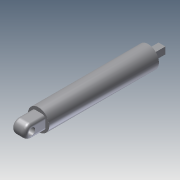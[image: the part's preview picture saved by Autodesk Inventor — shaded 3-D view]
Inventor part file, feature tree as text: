
AUTODESK INVENTOR PART (.ipt)
format: ipt  version: 2011 (Build 150239000, 239)  size: 170,496 bytes
history: native  units: in
note: dims shown in document units (in); Inventor stores cm internally (conversion verified against a paired STEP export)
features: extrude x11, sketch x11, fillet x2
ambient origin geometry x8: Origin, YZ Plane, XZ Plane, XY Plane, X Axis, Y Axis, Z Axis, Center Point
bodies: Solid1 (feature_tree)
feature tree (24):
  extrude  "Extrusion1"  Depth=0.5in TaperAngle=0.0deg
  extrude  "Extrusion2"  Depth=0.5in TaperAngle=0.0deg
  extrude  "Extrusion3"  Depth=0.5in TaperAngle=0.0deg
  extrude  "Extrusion4"  Depth=0.125in
  extrude  "Extrusion5"  Depth=0.25in
  extrude  "Extrusion6"  Depth=0.125in
  fillet  "Fillet1"  Radius=0.78in
  extrude  "Extrusion7"  Depth=4.0in TaperAngle=0.0deg
  extrude  "Extrusion8"  Depth=0.5in TaperAngle=0.0deg
  extrude  "Extrusion9"  Depth=0.5in TaperAngle=0.0deg
  extrude  "Extrusion10"  Depth=0.125in
  extrude  "Extrusion11"  [1 undecoded]
  fillet  "Fillet2"  [1 undecoded]
  sketch  "Sketch1"  dims[d0=4.0in d1=0.0in d2=0.5in d3=0.0in]
  sketch  "Sketch2"  dims[d4=0.25in d5=0.5in d6=0.0in]
  sketch  "Sketch3"  dims[d7=0.5in d8=0.0in d9=0.5in d10=0.0in]
  sketch  "Sketch4"  dims[d11=0.125in d12=0.125in]
  sketch  "Sketch5"  dims[d13=0.25in d14=0.25in]
  sketch  "Sketch6"  dims[d15=0.5in d16=0.0in d17=0.125in d18=0.78in]
  sketch  "Sketch7"  dims[d19=4.0in d20=0.0in d21=4.0in d22=0.0in]
  sketch  "Sketch8"  dims[d23=0.5in d24=0.5in d25=0.0in]
  sketch  "Sketch9"  dims[d26=0.25in d27=0.5in d28=0.0in]
  sketch  "Sketch10"  dims[d29=0.5in d30=0.0in d31=0.125in]
  sketch  "Sketch11"
note: 2 required parameter values undecoded (feature->parameter linkage not recoverable at this tier; creation-order binding heuristic only, values carry confidence <= 0.55)
